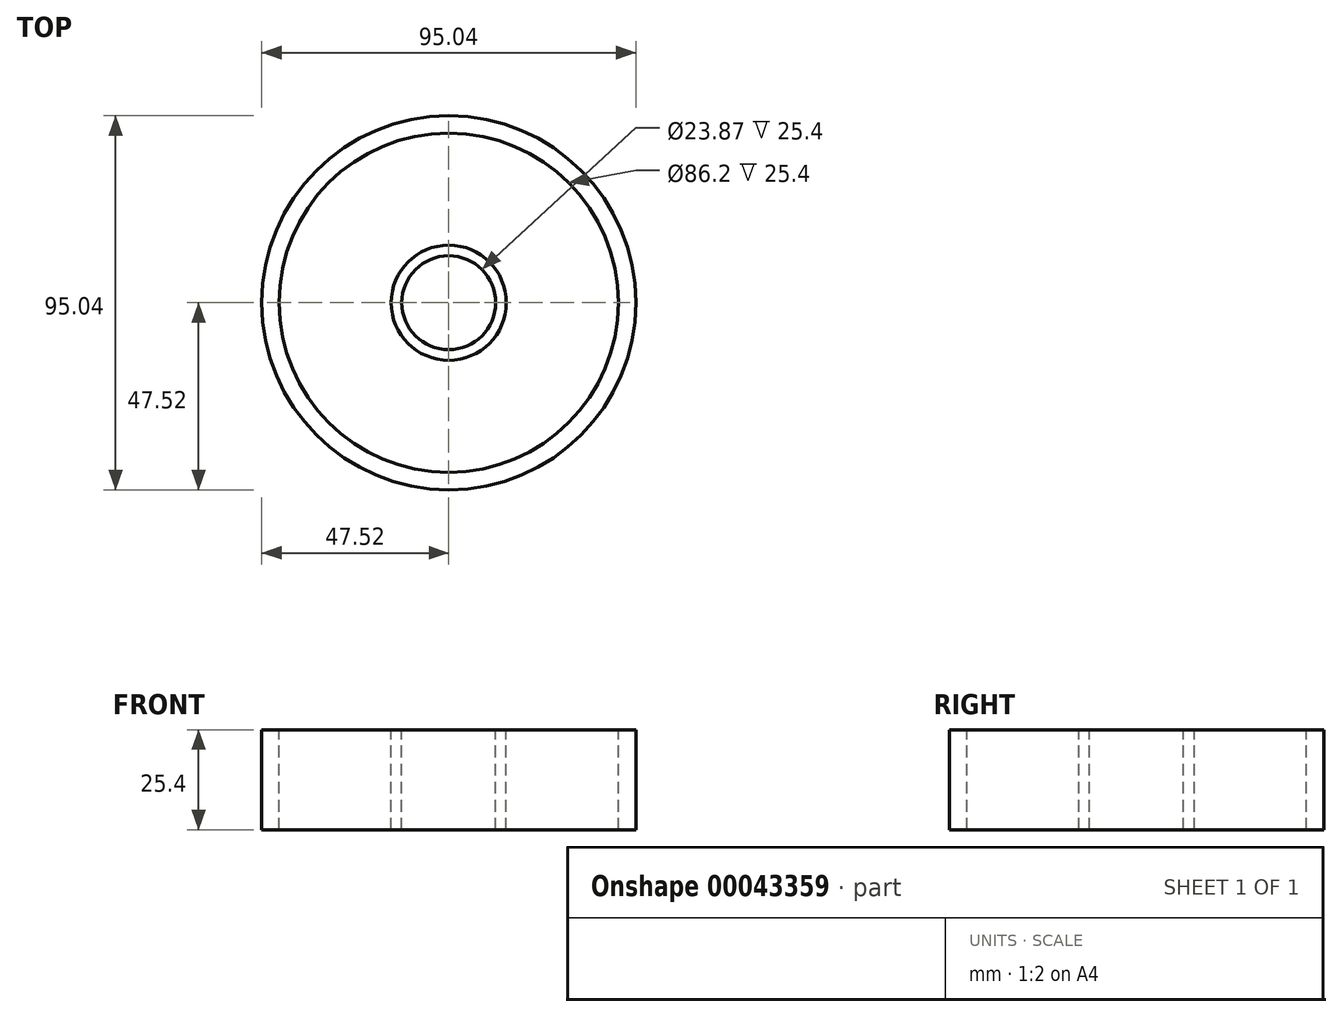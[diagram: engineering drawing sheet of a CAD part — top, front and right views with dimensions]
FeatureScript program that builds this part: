
annotation { "Feature Type Name" : "Feature", "Feature Type Description" : "" }
export const myFeature = defineFeature(function(context is Context, id is Id, definition is map)
    precondition{}
    {
        {
            var Q0;
            Q0=qCreatedBy(makeId("Top.planeOp"),FACE);
            var sketch = newSketch(context, id + "F0", { "sketchPlane" : qUnion([Q0])});
            skCircle(sketch, "E0", {"center": v(0, 0) * mm, "radius": 47.52 * mm});
            skSolve(sketch);
        }
        {
            var Q0;
            Q0=makeQuery(id+"F0.imprint","IMPRINT",FACE,{"disambiguationData":[TD([[makeQuery(id+"F0.imprint","IMPRINT",EDGE,{"derivedFrom":sQuery(id+"F0.wireOp",EDGE,"E0")}),1.0]])]});
            extrude(context, id + "F1", {"entities" : qUnion([Q0]), "oppositeDirection" : true, "depth" : 25.4 * mm});
        }
        {
            var Q0;
            Q0=makeQuery(id+"F1.opExtrude","CAP_FACE",FACE,{"disambiguationData":[OSD([sQuery(id+"F0.wireOp",EDGE,"E0")])],"isStart":true});
            var sketch = newSketch(context, id + "F2", { "sketchPlane" : qUnion([Q0])});
            skCircle(sketch, "E1", {"center": v(0, 0) * mm, "radius": 43.1 * mm});
            skSolve(sketch);
        }
        {
            var Q0;
            Q0=makeQuery(id+"F2.imprint","IMPRINT",FACE,{"disambiguationData":[TD([[makeQuery(id+"F2.imprint","IMPRINT",EDGE,{"derivedFrom":sQuery(id+"F2.wireOp",EDGE,"E1")}),1.0]])]});
            extrude(context, id + "F3", {"entities" : qUnion([Q0]), "operationType" : NewBodyOperationType.REMOVE, "oppositeDirection" : true, "depth" : 25.4 * mm});
        }
        {
            var Q0;
            Q0=qCreatedBy(makeId("Top.planeOp"),FACE);
            var sketch = newSketch(context, id + "F4", { "sketchPlane" : qUnion([Q0])});
            skCircle(sketch, "E2", {"center": v(0, 0) * mm, "radius": 14.62 * mm});
            skSolve(sketch);
        }
        {
            var Q0;
            Q0=makeQuery(id+"F4.imprint","IMPRINT",FACE,{"disambiguationData":[TD([[makeQuery(id+"F4.imprint","IMPRINT",EDGE,{"derivedFrom":sQuery(id+"F4.wireOp",EDGE,"E2")}),1.0]])]});
            var sketch = newSketch(context, id + "F5", { "sketchPlane" : qUnion([Q0])});
            skCircle(sketch, "E3", {"center": v(0, 0) * mm, "radius": 11.94 * mm});
            skSolve(sketch);
        }
        {
            var Q0;
            Q0=makeQuery(id+"F5.imprint","IMPRINT",FACE,{"disambiguationData":[TD([[makeQuery(id+"F5.imprint","IMPRINT",EDGE,{"derivedFrom":sQuery(id+"F5.wireOp",EDGE,"E3")}),-1.0]])]});
            extrude(context, id + "F6", {"entities" : qUnion([Q0]), "oppositeDirection" : true, "depth" : 25.4 * mm});
        }
    });
